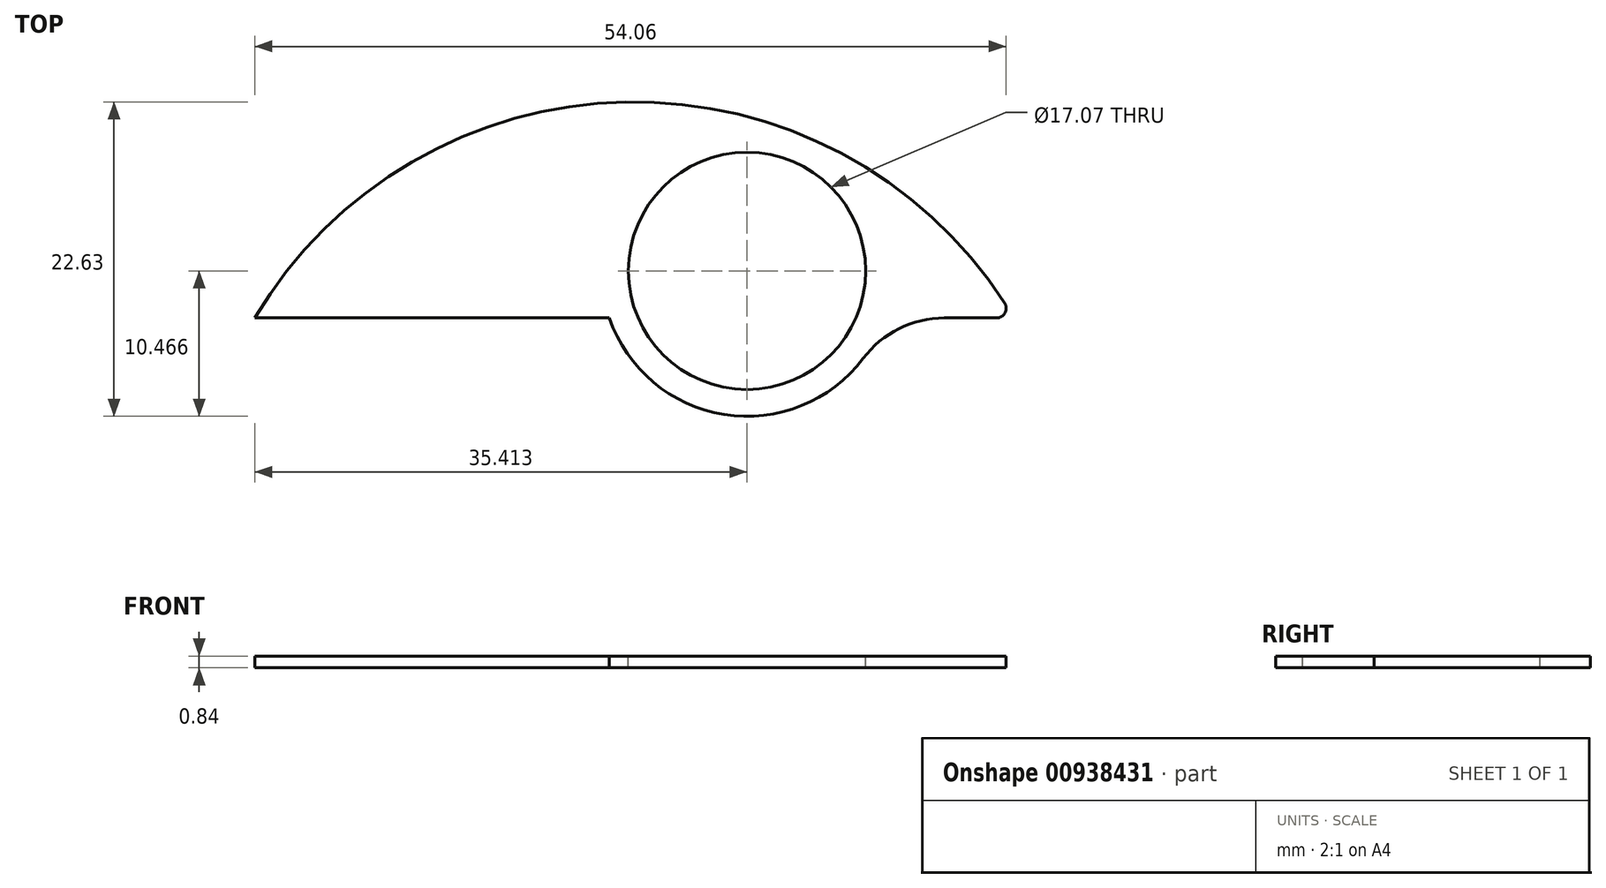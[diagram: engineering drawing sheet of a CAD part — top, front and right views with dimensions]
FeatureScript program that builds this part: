
annotation { "Feature Type Name" : "Feature", "Feature Type Description" : "" }
export const myFeature = defineFeature(function(context is Context, id is Id, definition is map)
    precondition{}
    {
        {
            var Q0;
            Q0=qCreatedBy(makeId("Top.planeOp"),FACE);
            var sketch = newSketch(context, id + "F0", { "sketchPlane" : qUnion([Q0])});
            skCircle(sketch, "E0", {"center": v(0, 0) * mm, "radius": 27.3 * mm});
            skSolve(sketch);
        }
        {
            var Q0;
            Q0 = qSketchRegion(id + "F0", true);
            extrude(context, id + "F1", {"entities" : qUnion([Q0]), "depth" : 0.84 * mm, "offsetDistance" : 25.4 * mm});
        }
        {
            var Q0;
            Q0=makeQuery(id+"F1.opExtrude","CAP_FACE",FACE,{"disambiguationData":[OSD([sQuery(id+"F0.wireOp",EDGE,"E0")])],"isStart":false});
            var sketch = newSketch(context, id + "F2", { "sketchPlane" : qUnion([Q0])});
            skLineSegment(sketch, "E1", {"start": v(-27.3, 0) * mm, "end": v(27.3, 0) * mm});
            skSolve(sketch);
        }
        {
            var Q0;
            {var subQ0=sQuery(id+"F2.wireOp",EDGE,"E1");Q0=makeQuery(id+"F2.imprint","IMPRINT",FACE,{"disambiguationData":[TD([[makeQuery(id+"F2.imprint","IMPRINT",EDGE,{"derivedFrom":subQ0}),-1.0]])]});}
            extrude(context, id + "F3", {"entities" : qUnion([Q0]), "operationType" : NewBodyOperationType.REMOVE, "oppositeDirection" : true, "depth" : 25.4 * mm, "offsetDistance" : 25.4 * mm});
        }
        {
            var Q0;
            Q0=makeQuery(id+"F1.opExtrude","CAP_FACE",FACE,{"disambiguationData":[OSD([sQuery(id+"F0.wireOp",EDGE,"E0")])],"isStart":false});
            var sketch = newSketch(context, id + "F4", { "sketchPlane" : qUnion([Q0])});
            skArc(sketch, "E2", {"start": v(27.3, 0) * mm, "mid": v(0, 15.55) * mm, "end": v(-27.3, 0) * mm});
            skSolve(sketch);
        }
        {
            var Q0;
            Q0=makeQuery(id+"F4.imprint","IMPRINT",FACE,{"disambiguationData":[TD([[makeQuery(id+"F4.imprint","IMPRINT",EDGE,{"derivedFrom":sQuery(id+"F4.wireOp",EDGE,"E2")}),-1.0]])]});
            extrude(context, id + "F5", {"entities" : qUnion([Q0]), "operationType" : NewBodyOperationType.REMOVE, "oppositeDirection" : true, "depth" : 25.4 * mm, "offsetDistance" : 25.4 * mm});
        }
        {
            var Q0;
            Q0=makeQuery(id+"F1.opExtrude","CAP_FACE",FACE,{"disambiguationData":[OSD([sQuery(id+"F0.wireOp",EDGE,"E0")])],"isStart":false});
            var sketch = newSketch(context, id + "F6", { "sketchPlane" : qUnion([Q0])});
            skCircle(sketch, "E3", {"center": v(8.1, 3.39) * mm, "radius": 10.46 * mm});
            skSolve(sketch);
        }
        {
            var Q0;
            {var subQ0=sQuery(id+"F6.wireOp",EDGE,"E3");var subQ1=makeQuery(id+"F3.boolean.opBoolean","COPY",EDGE,{"derivedFrom":makeQuery(id+"F3.opExtrude","CAP_EDGE",EDGE,{"disambiguationData":[OSD([sQuery(id+"F2.wireOp",EDGE,"E1")])],"isStart":true})});var subQ2=makeQuery(id+"F6.imprint","INTERSECT",VERTEX,{"disambiguationData":[OD(0.0)],"derivedFrom":[subQ1,subQ0]});Q0=makeQuery(id+"F6.imprint","IMPRINT",FACE,{"disambiguationData":[TD([[makeQuery(id+"F6.imprint","IMPRINT",EDGE,{"disambiguationData":[TD([[subQ2,1.0]])],"derivedFrom":subQ0}),1.0]])]});}
            var sketch = newSketch(context, id + "F7", { "sketchPlane" : qUnion([Q0])});
            skSolve(sketch);
        }
        {
            var Q0;
            {var subQ0=sQuery(id+"F6.wireOp",EDGE,"E3");var subQ1=makeQuery(id+"F3.boolean.opBoolean","COPY",EDGE,{"derivedFrom":makeQuery(id+"F3.opExtrude","CAP_EDGE",EDGE,{"disambiguationData":[OSD([sQuery(id+"F2.wireOp",EDGE,"E1")])],"isStart":true})});var subQ2=makeQuery(id+"F6.imprint","INTERSECT",VERTEX,{"disambiguationData":[OD(0.0)],"derivedFrom":[subQ1,subQ0]});Q0=makeQuery(id+"F7.imprint","IMPRINT",FACE,{"disambiguationData":[TD([[makeQuery(id+"F7.imprint","IMPRINT",EDGE,{"derivedFrom":makeQuery(id+"F6.imprint","IMPRINT",EDGE,{"disambiguationData":[TD([[subQ2,1.0]])],"derivedFrom":subQ0})}),1.0]])]});}
            var sketch = newSketch(context, id + "F8", { "sketchPlane" : qUnion([Q0])});
            skCircle(sketch, "E4.0", {"center": v(8.1, 3.39) * mm, "radius": 8.53 * mm});
            skSolve(sketch);
        }
        {
            var Q0;
            {var subQ0=sQuery(id+"F6.wireOp",EDGE,"E3");var subQ1=makeQuery(id+"F3.boolean.opBoolean","COPY",EDGE,{"derivedFrom":makeQuery(id+"F3.opExtrude","CAP_EDGE",EDGE,{"disambiguationData":[OSD([sQuery(id+"F2.wireOp",EDGE,"E1")])],"isStart":true})});var subQ2=makeQuery(id+"F6.imprint","INTERSECT",VERTEX,{"disambiguationData":[OD(0.0)],"derivedFrom":[subQ1,subQ0]});Q0=makeQuery(id+"F7.imprint","IMPRINT",FACE,{"disambiguationData":[TD([[makeQuery(id+"F7.imprint","IMPRINT",EDGE,{"derivedFrom":makeQuery(id+"F6.imprint","IMPRINT",EDGE,{"disambiguationData":[TD([[subQ2,1.0]])],"derivedFrom":subQ0})}),1.0]])]});}
            var Q1;
            {var subQ0=sQuery(id+"F6.wireOp",EDGE,"E3");var subQ1=makeQuery(id+"F3.boolean.opBoolean","COPY",EDGE,{"derivedFrom":makeQuery(id+"F3.opExtrude","CAP_EDGE",EDGE,{"disambiguationData":[OSD([sQuery(id+"F2.wireOp",EDGE,"E1")])],"isStart":true})});var subQ2=makeQuery(id+"F6.imprint","INTERSECT",VERTEX,{"disambiguationData":[OD(0.0)],"derivedFrom":[subQ1,subQ0]});Q1=makeQuery(id+"F6.imprint","IMPRINT",FACE,{"disambiguationData":[TD([[makeQuery(id+"F6.imprint","IMPRINT",EDGE,{"disambiguationData":[TD([[subQ2,-1.0]])],"derivedFrom":subQ0}),1.0]])]});}
            extrude(context, id + "F9", {"entities" : qUnion([Q0, Q1]), "operationType" : NewBodyOperationType.ADD, "oppositeDirection" : true, "depth" : 0.84 * mm, "offsetDistance" : 25.4 * mm});
        }
        {
            var Q0;
            {var subQ0=sQuery(id+"F8.wireOp",EDGE,"E4.0");var subQ1=sQuery(id+"F6.wireOp",EDGE,"E3");var subQ2=makeQuery(id+"F3.boolean.opBoolean","COPY",EDGE,{"derivedFrom":makeQuery(id+"F3.opExtrude","CAP_EDGE",EDGE,{"disambiguationData":[OSD([sQuery(id+"F2.wireOp",EDGE,"E1")])],"isStart":true})});var subQ3=makeQuery(id+"F7.imprint","IMPRINT",EDGE,{"derivedFrom":makeQuery(id+"F6.imprint","IMPRINT",EDGE,{"disambiguationData":[TD([[makeQuery(id+"F6.imprint","INTERSECT",VERTEX,{"disambiguationData":[OD(0.0)],"derivedFrom":[subQ2,subQ1]}),-1.0]])],"derivedFrom":subQ2})});var subQ4=makeQuery(id+"F8.imprint","INTERSECT",VERTEX,{"disambiguationData":[OD(0.0)],"derivedFrom":[subQ3,subQ0]});Q0=makeQuery(id+"F8.imprint","IMPRINT",FACE,{"disambiguationData":[TD([[makeQuery(id+"F8.imprint","IMPRINT",EDGE,{"disambiguationData":[TD([[subQ4,1.0]])],"derivedFrom":subQ0}),1.0]])]});}
            var Q1;
            {var subQ0=sQuery(id+"F8.wireOp",EDGE,"E4.0");var subQ1=sQuery(id+"F6.wireOp",EDGE,"E3");var subQ2=makeQuery(id+"F3.boolean.opBoolean","COPY",EDGE,{"derivedFrom":makeQuery(id+"F3.opExtrude","CAP_EDGE",EDGE,{"disambiguationData":[OSD([sQuery(id+"F2.wireOp",EDGE,"E1")])],"isStart":true})});var subQ3=makeQuery(id+"F7.imprint","IMPRINT",EDGE,{"derivedFrom":makeQuery(id+"F6.imprint","IMPRINT",EDGE,{"disambiguationData":[TD([[makeQuery(id+"F6.imprint","INTERSECT",VERTEX,{"disambiguationData":[OD(0.0)],"derivedFrom":[subQ2,subQ1]}),-1.0]])],"derivedFrom":subQ2})});var subQ4=makeQuery(id+"F8.imprint","INTERSECT",VERTEX,{"disambiguationData":[OD(0.0)],"derivedFrom":[subQ3,subQ0]});Q1=makeQuery(id+"F8.imprint","IMPRINT",FACE,{"disambiguationData":[TD([[makeQuery(id+"F8.imprint","IMPRINT",EDGE,{"disambiguationData":[TD([[subQ4,-1.0]])],"derivedFrom":subQ0}),1.0]])]});}
            extrude(context, id + "F10", {"entities" : qUnion([Q0, Q1]), "operationType" : NewBodyOperationType.REMOVE, "oppositeDirection" : true, "depth" : 17.58 * mm, "offsetDistance" : 25.4 * mm});
        }
        {
            var Q0;
            {var subQ0=sQuery(id+"F6.wireOp",EDGE,"E3");var subQ1=sQuery(id+"F2.wireOp",EDGE,"E1");var subQ2=makeQuery(id+"F3.boolean.opBoolean","COPY",EDGE,{"derivedFrom":makeQuery(id+"F3.opExtrude","CAP_EDGE",EDGE,{"disambiguationData":[OSD([subQ1])],"isStart":true})});var subQ3=makeQuery(id+"F6.imprint","INTERSECT",VERTEX,{"disambiguationData":[OD(0.0)],"derivedFrom":[subQ2,subQ0]});Q0=makeQuery(id+"F9.boolean.opBoolean","INTERSECT",EDGE,{"disambiguationData":[OD(1.0)],"derivedFrom":[makeQuery(id+"F3.boolean.opBoolean","COPY",FACE,{"derivedFrom":makeQuery(id+"F3.opExtrude","SWEPT_FACE",FACE,{"disambiguationData":[OSD([subQ1])]})}),makeQuery(id+"F9.opExtrude","SWEPT_FACE",FACE,{"disambiguationData":[OSD([subQ0]),TDD([makeQuery(id+"F6.imprint","IMPRINT",EDGE,{"disambiguationData":[TD([[subQ3,-1.0]])],"derivedFrom":subQ0})])]}),makeQuery(id+"F9.opExtrude","SWEPT_FACE",FACE,{"disambiguationData":[OSD([subQ0]),TDD([makeQuery(id+"F7.imprint","IMPRINT",EDGE,{"derivedFrom":makeQuery(id+"F6.imprint","IMPRINT",EDGE,{"disambiguationData":[TD([[subQ3,1.0]])],"derivedFrom":subQ0})})])]})]});}
            fillet(context, id + "F11", {"entities" : qUnion([Q0]), "radius" : 7.3 * mm, "tangentPropagation" : true, "allowEdgeOverflow" : false});
        }
        {
            var Q0;
            {var subQ0=sQuery(id+"F4.wireOp",EDGE,"E2");var subQ1=sQuery(id+"F0.wireOp",EDGE,"E0");var subQ2=makeQuery(id+"F1.opExtrude","CAP_EDGE",EDGE,{"disambiguationData":[OSD([subQ1])],"isStart":false});var subQ3=sQuery(id+"F2.wireOp",EDGE,"E1");Q0=makeQuery(id+"F5.boolean.opBoolean","MERGE",EDGE,{"derivedFrom":[makeQuery(id+"F3.boolean.opBoolean","COPY",EDGE,{"derivedFrom":makeQuery(id+"F3.opExtrude","SWEPT_EDGE",EDGE,{"disambiguationData":[OSD([subQ1,subQ3]),TDD([makeQuery(id+"F2.imprint","INTERSECT",VERTEX,{"disambiguationData":[OD(1.0)],"derivedFrom":[subQ2,subQ3]})])]})})],"fromTools":[makeQuery(id+"F5.opExtrude","SWEPT_EDGE",EDGE,{"disambiguationData":[OSD([subQ1,subQ3,subQ0]),TDD([makeQuery(id+"F4.imprint","INTERSECT",VERTEX,{"disambiguationData":[OD(1.0)],"derivedFrom":[makeQuery(id+"F3.boolean.opBoolean","COPY",EDGE,{"derivedFrom":makeQuery(id+"F3.opExtrude","CAP_EDGE",EDGE,{"disambiguationData":[OSD([subQ3])],"isStart":true})}),subQ2,subQ0]})])]})]});}
            fillet(context, id + "F12", {"entities" : qUnion([Q0]), "radius" : 0.7 * mm, "tangentPropagation" : true, "allowEdgeOverflow" : false});
        }
    });
